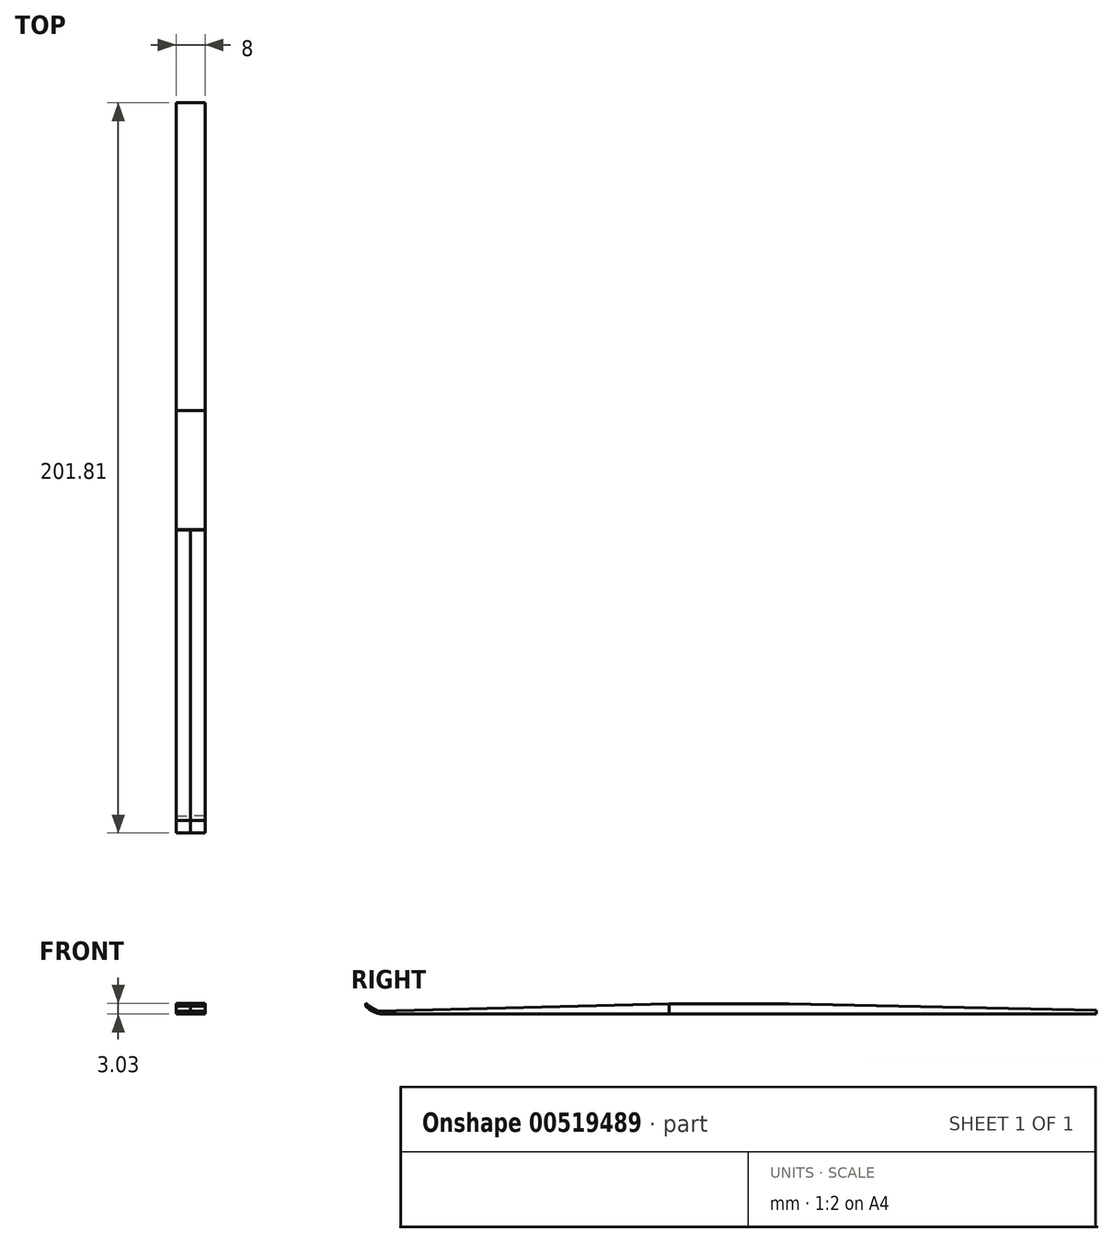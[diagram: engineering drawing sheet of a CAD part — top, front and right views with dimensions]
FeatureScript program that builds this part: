
annotation { "Feature Type Name" : "Feature", "Feature Type Description" : "" }
export const myFeature = defineFeature(function(context is Context, id is Id, definition is map)
    precondition{}
    {
        {
            var Q0;
            Q0=qCreatedBy(makeId("Front.planeOp"),FACE);
            var sketch = newSketch(context, id + "F0", { "sketchPlane" : qUnion([Q0])});
            skLineSegment(sketch, "E0.bottom", {"start": v(-4, 1.4) * mm, "end": v(4, 1.4) * mm});
            skLineSegment(sketch, "E0.top", {"start": v(-4, -1.4) * mm, "end": v(4, -1.4) * mm});
            skLineSegment(sketch, "E0.left", {"start": v(-4, 1.4) * mm, "end": v(-4, -1.4) * mm});
            skLineSegment(sketch, "E0.right", {"start": v(4, 1.4) * mm, "end": v(4, -1.4) * mm});
            skPoint(sketch, "E0.middle", {"position": v(0, 0) * mm});
            skSolve(sketch);
        }
        {
            var Q0;
            Q0 = qSketchRegion(id + "F0", true);
            extrude(context, id + "F1", {"entities" : qUnion([Q0]), "depth" : 16.5 * mm, "offsetDistance" : 25 * mm});
        }
        {
            var Q0;
            Q0=makeQuery(id+"F0.imprint","IMPRINT",FACE,{"disambiguationData":[TD([[makeQuery(id+"F0.imprint","IMPRINT",EDGE,{"derivedFrom":sQuery(id+"F0.wireOp",EDGE,"E0.bottom")}),-1.0]])]});
            extrude(context, id + "F2", {"entities" : qUnion([Q0]), "operationType" : NewBodyOperationType.ADD, "oppositeDirection" : true, "depth" : 16.5 * mm, "offsetDistance" : 25 * mm});
        }
        {
            var Q0;
            Q0=qCreatedBy(makeId("Right.planeOp"),FACE);
            var sketch = newSketch(context, id + "F3", { "sketchPlane" : qUnion([Q0])});
            skLineSegment(sketch, "E1", {"start": v(-16.5, -1.4) * mm, "end": v(-98.5, -1.4) * mm});
            skLineSegment(sketch, "E2", {"start": v(16.5, 1.4) * mm, "end": v(16.5, -1.4) * mm});
            skLineSegment(sketch, "E3", {"start": v(16.5, -1.4) * mm, "end": v(101.5, -1.4) * mm});
            skLineSegment(sketch, "E4", {"start": v(101.5, -1.4) * mm, "end": v(101.5, -0.4) * mm});
            skLineSegment(sketch, "E5", {"start": v(101.5, -0.4) * mm, "end": v(16.5, 1.4) * mm});
            skLineSegment(sketch, "E6", {"start": v(-98.5, -1.4) * mm, "end": v(-98.5, -0.6) * mm});
            skLineSegment(sketch, "E7", {"start": v(-98.5, -0.6) * mm, "end": v(-16.5, 1.4) * mm});
            skArc(sketch, "E8", {"start": v(-100.3, 0.83) * mm, "mid": v(-97.76, -0.92) * mm, "end": v(-94.71, -1.4) * mm});
            skLineSegment(sketch, "E9", {"start": v(-100.3, 0.83) * mm, "end": v(-100.3, 1.63) * mm});
            skArc(sketch, "E10", {"start": v(-100.3, 1.63) * mm, "mid": v(-96.88, -0.54) * mm, "end": v(-92.92, -1.4) * mm});
            skLineSegment(sketch, "E11", {"start": v(-16.5, 1.4) * mm, "end": v(-16.5, -1.4) * mm});
            skSolve(sketch);
        }
        {
            var Q0;
            Q0=makeQuery(id+"F3.imprint","IMPRINT",FACE,{"disambiguationData":[TD([[makeQuery(id+"F3.imprint","IMPRINT",EDGE,{"derivedFrom":sQuery(id+"F3.wireOp",EDGE,"E2")}),1.0]])]});
            var Q1;
            {var subQ5=sQuery(id+"F3.wireOp",EDGE,"ZL5HCL6I-8sDr-qLXJ-Qw0q-pt8eyXDb5g0s");Q1=makeQuery(id+"F3.imprint","IMPRINT",FACE,{"disambiguationData":[TD([[makeQuery(id+"F3.imprint","IMPRINT",EDGE,{"derivedFrom":subQ5}),-1.0]])]});}
            var Q2;
            {var subQ0=sQuery(id+"F3.wireOp",EDGE,"E8");var subQ1=sQuery(id+"F3.wireOp",EDGE,"E1");var subQ2=makeQuery(id+"F3.imprint","INTERSECT",VERTEX,{"derivedFrom":[subQ1,subQ0]});Q2=makeQuery(id+"F3.imprint","IMPRINT",FACE,{"disambiguationData":[TD([[makeQuery(id+"F3.imprint","IMPRINT",EDGE,{"disambiguationData":[TD([[subQ2,1.0]])],"derivedFrom":subQ1}),-1.0]])]});}
            extrude(context, id + "F4", {"entities" : qUnion([Q0, Q1, Q2]), "operationType" : NewBodyOperationType.ADD, "depth" : 4 * mm, "offsetDistance" : 25 * mm});
        }
        {
            var Q0;
            Q0=makeQuery(id+"F3.imprint","IMPRINT",FACE,{"disambiguationData":[TD([[makeQuery(id+"F3.imprint","IMPRINT",EDGE,{"derivedFrom":sQuery(id+"F3.wireOp",EDGE,"E2")}),1.0]])]});
            var Q1;
            {var subQ0=sQuery(id+"F3.wireOp",EDGE,"E8");var subQ1=sQuery(id+"F3.wireOp",EDGE,"E1");var subQ2=makeQuery(id+"F3.imprint","INTERSECT",VERTEX,{"derivedFrom":[subQ1,subQ0]});Q1=makeQuery(id+"F3.imprint","IMPRINT",FACE,{"disambiguationData":[TD([[makeQuery(id+"F3.imprint","IMPRINT",EDGE,{"disambiguationData":[TD([[subQ2,1.0]])],"derivedFrom":subQ1}),-1.0]])]});}
            var Q2;
            {var subQ5=sQuery(id+"F3.wireOp",EDGE,"ZL5HCL6I-8sDr-qLXJ-Qw0q-pt8eyXDb5g0s");Q2=makeQuery(id+"F3.imprint","IMPRINT",FACE,{"disambiguationData":[TD([[makeQuery(id+"F3.imprint","IMPRINT",EDGE,{"derivedFrom":subQ5}),-1.0]])]});}
            extrude(context, id + "F5", {"entities" : qUnion([Q0, Q1, Q2]), "operationType" : NewBodyOperationType.ADD, "oppositeDirection" : true, "depth" : 4 * mm, "offsetDistance" : 25 * mm});
        }
        {
            var Q0;
            {var subQ0=sQuery(id+"F3.wireOp",EDGE,"E11");Q0=makeQuery(id+"F3.imprint","IMPRINT",FACE,{"disambiguationData":[TD([[makeQuery(id+"F3.imprint","IMPRINT",EDGE,{"derivedFrom":subQ0}),-1.0]])]});}
            var Q1;
            {var subQ5=sQuery(id+"F3.wireOp",EDGE,"E9");Q1=makeQuery(id+"F3.imprint","IMPRINT",FACE,{"disambiguationData":[TD([[makeQuery(id+"F3.imprint","IMPRINT",EDGE,{"derivedFrom":subQ5}),-1.0]])]});}
            var Q2;
            {var subQ0=sQuery(id+"F3.wireOp",EDGE,"E8");var subQ1=sQuery(id+"F3.wireOp",EDGE,"E1");var subQ5=makeQuery(id+"F3.imprint","INTERSECT",VERTEX,{"disambiguationData":[OD(0.0)],"derivedFrom":[subQ1,subQ0]});Q2=makeQuery(id+"F3.imprint","IMPRINT",FACE,{"disambiguationData":[TD([[makeQuery(id+"F3.imprint","IMPRINT",EDGE,{"disambiguationData":[TD([[subQ5,1.0]])],"derivedFrom":subQ1}),-1.0]])]});}
            extrude(context, id + "F6", {"entities" : qUnion([Q0, Q1, Q2]), "depth" : 4 * mm, "offsetDistance" : 25 * mm});
        }
        {
            var Q0;
            {var subQ0=sQuery(id+"F3.wireOp",EDGE,"E11");Q0=makeQuery(id+"F3.imprint","IMPRINT",FACE,{"disambiguationData":[TD([[makeQuery(id+"F3.imprint","IMPRINT",EDGE,{"derivedFrom":subQ0}),-1.0]])]});}
            var Q1;
            {var subQ5=sQuery(id+"F3.wireOp",EDGE,"E9");Q1=makeQuery(id+"F3.imprint","IMPRINT",FACE,{"disambiguationData":[TD([[makeQuery(id+"F3.imprint","IMPRINT",EDGE,{"derivedFrom":subQ5}),-1.0]])]});}
            var Q2;
            {var subQ0=sQuery(id+"F3.wireOp",EDGE,"E8");var subQ1=sQuery(id+"F3.wireOp",EDGE,"E1");var subQ5=makeQuery(id+"F3.imprint","INTERSECT",VERTEX,{"disambiguationData":[OD(0.0)],"derivedFrom":[subQ1,subQ0]});Q2=makeQuery(id+"F3.imprint","IMPRINT",FACE,{"disambiguationData":[TD([[makeQuery(id+"F3.imprint","IMPRINT",EDGE,{"disambiguationData":[TD([[subQ5,1.0]])],"derivedFrom":subQ1}),-1.0]])]});}
            extrude(context, id + "F7", {"entities" : qUnion([Q0, Q1, Q2]), "oppositeDirection" : true, "depth" : 4 * mm, "offsetDistance" : 25 * mm});
        }
    });
